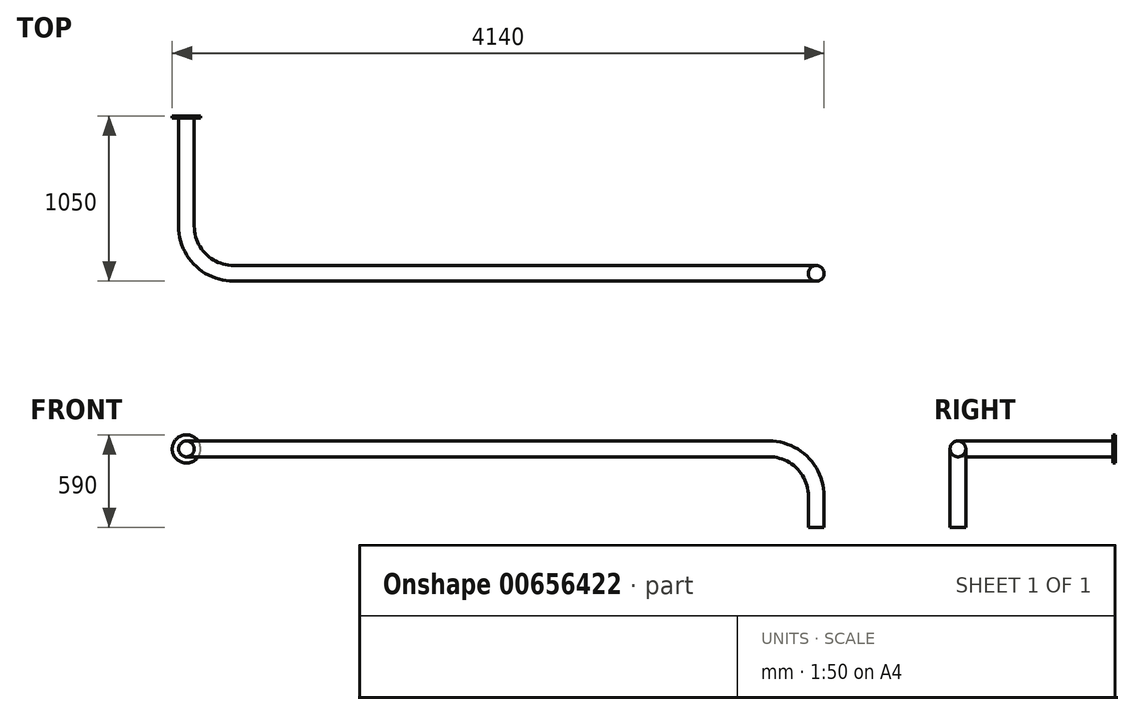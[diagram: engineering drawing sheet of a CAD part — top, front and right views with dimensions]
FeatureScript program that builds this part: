
annotation { "Feature Type Name" : "Feature", "Feature Type Description" : "" }
export const myFeature = defineFeature(function(context is Context, id is Id, definition is map)
    precondition{}
    {
        {
            var Q0;
            Q0=qCreatedBy(makeId("Top.planeOp"),FACE);
            var sketch = newSketch(context, id + "F0", { "sketchPlane" : qUnion([Q0])});
            skLineSegment(sketch, "E0", {"start": v(0, 0) * mm, "end": v(0, -700) * mm});
            skLineSegment(sketch, "E1", {"start": v(300, -1000) * mm, "end": v(4000, -1000) * mm});
            skPoint(sketch, "E2.visualSharp", {"position": v(0, -1000) * mm});
            skArc(sketch, "E2.filletArc", {"start": v(0, -700) * mm, "mid": v(87.87, -912.13) * mm, "end": v(300, -1000) * mm});
            skSolve(sketch);
        }
        {
            var Q0;
            Q0=qCreatedBy(makeId("Front.planeOp"),FACE);
            var sketch = newSketch(context, id + "F1", { "sketchPlane" : qUnion([Q0])});
            skCircle(sketch, "E3", {"center": v(0, 0) * mm, "radius": 50 * mm});
            skCircle(sketch, "E4", {"center": v(0, 0) * mm, "radius": 90 * mm});
            skSolve(sketch);
        }
        {
            var Q0;
            Q0=qCreatedBy(makeId("Front.planeOp"),FACE);
            cPlane(context, id + "F2", {"entities" : qUnion([Q0]), "cplaneType" : CPlaneType.OFFSET, "offset" : 1000 * mm, "width" : 150 * mm, "height" : 150 * mm});
        }
        {
            var Q0;
            Q0=qCreatedBy(id+"F2.planeOp",FACE);
            var sketch = newSketch(context, id + "F3", { "sketchPlane" : qUnion([Q0])});
            skPoint(sketch, "E5.0", {"position": v(4000, 0) * mm});
            skLineSegment(sketch, "E6.0", {"start": v(300, 0) * mm, "end": v(3700, 0) * mm});
            skLineSegment(sketch, "E7", {"start": v(4000, -300) * mm, "end": v(4000, -500) * mm});
            skArc(sketch, "E8.filletArc", {"start": v(4000, -300) * mm, "mid": v(3912.13, -87.87) * mm, "end": v(3700, 0) * mm});
            skSolve(sketch);
        }
        {
            var Q0;
            Q0=makeQuery(id+"F1.imprint","IMPRINT",FACE,{"disambiguationData":[TD([[makeQuery(id+"F1.imprint","IMPRINT",EDGE,{"derivedFrom":sQuery(id+"F1.wireOp",EDGE,"E3")}),1.0]])]});
            var Q1;
            Q1=sQuery(id+"F0.wireOp",EDGE,"E0");
            var Q2;
            Q2=sQuery(id+"F0.wireOp",EDGE,"E2.filletArc");
            var Q3;
            Q3=sQuery(id+"F3.wireOp",EDGE,"E6.0");
            var Q4;
            Q4=sQuery(id+"F3.wireOp",EDGE,"E8.filletArc");
            var Q5;
            Q5=sQuery(id+"F3.wireOp",EDGE,"E7");
            sweep(context, id + "F4", {"profiles" : qUnion([Q0]), "path" : qUnion([Q1, Q2, Q3, Q4, Q5])});
        }
        {
            var Q0;
            Q0=makeQuery(id+"F1.imprint","IMPRINT",FACE,{"disambiguationData":[TD([[makeQuery(id+"F1.imprint","IMPRINT",EDGE,{"derivedFrom":sQuery(id+"F1.wireOp",EDGE,"E3")}),-1.0]])]});
            extrude(context, id + "F5", {"entities" : qUnion([Q0]), "operationType" : NewBodyOperationType.ADD, "depth" : 15 * mm, "offsetDistance" : 25 * mm});
        }
    });
